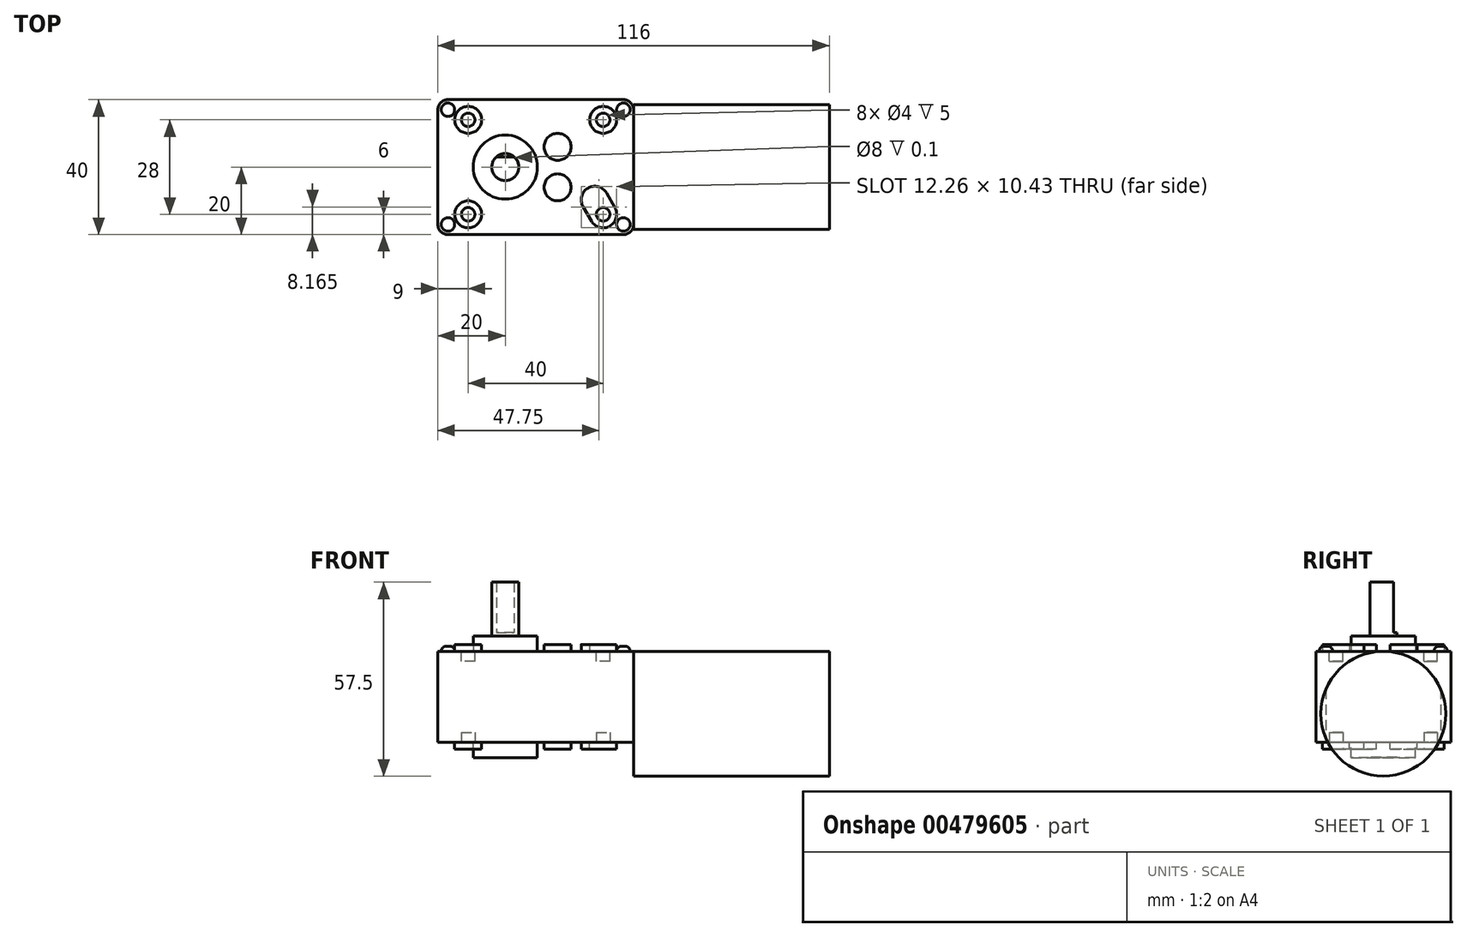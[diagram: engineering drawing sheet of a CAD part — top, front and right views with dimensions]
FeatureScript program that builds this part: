
annotation { "Feature Type Name" : "Feature", "Feature Type Description" : "" }
export const myFeature = defineFeature(function(context is Context, id is Id, definition is map)
    precondition{}
    {
        {
            var Q0;
            Q0=qCreatedBy(makeId("Top.planeOp"),FACE);
            var sketch = newSketch(context, id + "F0", { "sketchPlane" : qUnion([Q0])});
            skLineSegment(sketch, "E0.bottom", {"start": v(35, 20) * mm, "end": v(-17, 20) * mm});
            skLineSegment(sketch, "E0.top", {"start": v(35, -20) * mm, "end": v(-17, -20) * mm});
            skLineSegment(sketch, "E0.left", {"start": v(38, 17) * mm, "end": v(38, -17) * mm});
            skLineSegment(sketch, "E0.right", {"start": v(-20, 17) * mm, "end": v(-20, -17) * mm});
            skPoint(sketch, "E0.middle", {"position": v(9, 0) * mm});
            skPoint(sketch, "E1.visualSharp", {"position": v(-20, 20) * mm});
            skArc(sketch, "E1.filletArc", {"start": v(-17, 20) * mm, "mid": v(-19.12, 19.12) * mm, "end": v(-20, 17) * mm});
            skPoint(sketch, "E2.visualSharp", {"position": v(-20, -20) * mm});
            skArc(sketch, "E2.filletArc", {"start": v(-20, -17) * mm, "mid": v(-19.12, -19.12) * mm, "end": v(-17, -20) * mm});
            skPoint(sketch, "E3.visualSharp", {"position": v(38, -20) * mm});
            skArc(sketch, "E3.filletArc", {"start": v(35, -20) * mm, "mid": v(37.12, -19.12) * mm, "end": v(38, -17) * mm});
            skPoint(sketch, "E4.visualSharp", {"position": v(38, 20) * mm});
            skArc(sketch, "E4.filletArc", {"start": v(38, 17) * mm, "mid": v(37.12, 19.12) * mm, "end": v(35, 20) * mm});
            skSolve(sketch);
        }
        {
            var Q0;
            Q0 = qSketchRegion(id + "F0", true);
            extrude(context, id + "F1", {"entities" : qUnion([Q0]), "depth" : 27 * mm});
        }
        {
            var Q0;
            Q0=makeQuery(id+"F1.opExtrude","CAP_FACE",FACE,{"disambiguationData":[OSD([sQuery(id+"F0.wireOp",EDGE,"E0.bottom"),sQuery(id+"F0.wireOp",EDGE,"E0.top"),sQuery(id+"F0.wireOp",EDGE,"E0.left"),sQuery(id+"F0.wireOp",EDGE,"E0.right"),sQuery(id+"F0.wireOp",EDGE,"E1.filletArc"),sQuery(id+"F0.wireOp",EDGE,"E2.filletArc"),sQuery(id+"F0.wireOp",EDGE,"E3.filletArc"),sQuery(id+"F0.wireOp",EDGE,"E4.filletArc")])],"isStart":false});
            var sketch = newSketch(context, id + "F2", { "sketchPlane" : qUnion([Q0])});
            skLineSegment(sketch, "E5.bottom", {"start": v(-11, 14) * mm, "end": v(29, 14) * mm, "construction": true});
            skLineSegment(sketch, "E5.top", {"start": v(-11, -14) * mm, "end": v(29, -14) * mm, "construction": true});
            skLineSegment(sketch, "E5.left", {"start": v(-11, 14) * mm, "end": v(-11, -14) * mm, "construction": true});
            skLineSegment(sketch, "E5.right", {"start": v(29, 14) * mm, "end": v(29, -14) * mm, "construction": true});
            skPoint(sketch, "E5.middle", {"position": v(9, 0) * mm});
            skPoint(sketch, "E5.middle.positionSnap0", {"position": v(9, 20) * mm});
            skPoint(sketch, "E5.centerSnap0", {"position": v(9, 20) * mm});
            skCircle(sketch, "E6", {"center": v(-11, 14) * mm, "radius": 4 * mm});
            skCircle(sketch, "E7", {"center": v(29, 14) * mm, "radius": 4 * mm});
            skCircle(sketch, "E8", {"center": v(-11, -14) * mm, "radius": 4 * mm});
            skArc(sketch, "E9", {"start": v(29.96, -7.67) * mm, "mid": v(24.5, -6.2) * mm, "end": v(23.04, -11.67) * mm});
            skLineSegment(sketch, "E10", {"start": v(23.04, -11.67) * mm, "end": v(25.54, -16) * mm});
            skArc(sketch, "E11.trimOffspring", {"start": v(25.54, -16) * mm, "mid": v(31, -17.46) * mm, "end": v(32.46, -12) * mm});
            skLineSegment(sketch, "E12.trimOffspring", {"start": v(29.96, -7.67) * mm, "end": v(32.46, -12) * mm});
            skLineSegment(sketch, "E13", {"start": v(15.5, 14) * mm, "end": v(15.5, -14) * mm, "construction": true});
            skCircle(sketch, "E14", {"center": v(15.5, 6) * mm, "radius": 4 * mm});
            skCircle(sketch, "E15", {"center": v(15.5, -6) * mm, "radius": 4 * mm});
            skSolve(sketch);
        }
        {
            var Q0;
            Q0 = qSketchRegion(id + "F2", true);
            extrude(context, id + "F3", {"entities" : qUnion([Q0]), "operationType" : NewBodyOperationType.ADD, "depth" : 2 * mm});
        }
        {
            var Q0;
            Q0 = qSketchRegion(id + "F2", true);
            extrude(context, id + "F4", {"entities" : qUnion([Q0]), "operationType" : NewBodyOperationType.ADD, "oppositeDirection" : true, "depth" : 29 * mm});
        }
        {
            var Q0;
            Q0=makeQuery(id+"F1.opExtrude","CAP_FACE",FACE,{"disambiguationData":[OSD([sQuery(id+"F0.wireOp",EDGE,"E0.bottom"),sQuery(id+"F0.wireOp",EDGE,"E0.top"),sQuery(id+"F0.wireOp",EDGE,"E0.left"),sQuery(id+"F0.wireOp",EDGE,"E0.right"),sQuery(id+"F0.wireOp",EDGE,"E1.filletArc"),sQuery(id+"F0.wireOp",EDGE,"E2.filletArc"),sQuery(id+"F0.wireOp",EDGE,"E3.filletArc"),sQuery(id+"F0.wireOp",EDGE,"E4.filletArc")])],"isStart":false});
            var sketch = newSketch(context, id + "F5", { "sketchPlane" : qUnion([Q0])});
            skCircle(sketch, "E16", {"center": v(0, 0) * mm, "radius": 9.5 * mm});
            skSolve(sketch);
        }
        {
            var Q0;
            Q0 = qSketchRegion(id + "F5", true);
            extrude(context, id + "F6", {"entities" : qUnion([Q0]), "operationType" : NewBodyOperationType.ADD, "depth" : 4.5 * mm});
        }
        {
            var Q0;
            Q0 = qSketchRegion(id + "F5", true);
            extrude(context, id + "F7", {"entities" : qUnion([Q0]), "operationType" : NewBodyOperationType.ADD, "oppositeDirection" : true, "depth" : 31.5 * mm});
        }
        {
            var Q0;
            Q0=makeQuery(id+"F6.opExtrude","CAP_FACE",FACE,{"disambiguationData":[OSD([sQuery(id+"F5.wireOp",EDGE,"E16")])],"isStart":false});
            var sketch = newSketch(context, id + "F8", { "sketchPlane" : qUnion([Q0])});
            skCircle(sketch, "E17", {"center": v(0, 0) * mm, "radius": 4 * mm});
            skSolve(sketch);
        }
        {
            var Q0;
            Q0 = qSketchRegion(id + "F8", true);
            extrude(context, id + "F9", {"entities" : qUnion([Q0]), "operationType" : NewBodyOperationType.ADD, "depth" : 1 * mm});
        }
        {
            var Q0;
            Q0=makeQuery(id+"F9.opExtrude","CAP_FACE",FACE,{"disambiguationData":[OSD([sQuery(id+"F8.wireOp",EDGE,"E17")])],"isStart":false});
            var sketch = newSketch(context, id + "F10", { "sketchPlane" : qUnion([Q0])});
            skArc(sketch, "E18", {"start": v(-2.65, 3) * mm, "mid": v(0, -4) * mm, "end": v(2.65, 3) * mm});
            skLineSegment(sketch, "E19", {"start": v(-2.65, 3) * mm, "end": v(2.65, 3) * mm});
            skSolve(sketch);
        }
        {
            var Q0;
            Q0 = qSketchRegion(id + "F10", true);
            extrude(context, id + "F11", {"entities" : qUnion([Q0]), "operationType" : NewBodyOperationType.ADD, "depth" : 15 * mm});
        }
        {
            var Q0;
            Q0=makeQuery(id+"F7.opExtrude","CAP_FACE",FACE,{"disambiguationData":[OSD([sQuery(id+"F5.wireOp",EDGE,"E16")])],"isStart":false});
            var sketch = newSketch(context, id + "F12", { "sketchPlane" : qUnion([Q0])});
            skCircle(sketch, "E20", {"center": v(0, 0) * mm, "radius": 4 * mm});
            skSolve(sketch);
        }
        {
            var Q0;
            Q0 = qSketchRegion(id + "F12", true);
            extrude(context, id + "F13", {"entities" : qUnion([Q0]), "operationType" : NewBodyOperationType.REMOVE, "oppositeDirection" : true, "depth" : 0.1 * mm});
        }
        {
            var Q0;
            Q0=makeQuery(id+"F1.opExtrude","SWEPT_FACE",FACE,{"disambiguationData":[OSD([sQuery(id+"F0.wireOp",EDGE,"E0.left")])]});
            var sketch = newSketch(context, id + "F14", { "sketchPlane" : qUnion([Q0])});
            skCircle(sketch, "E21", {"center": v(0, 8.5) * mm, "radius": 18.5 * mm});
            skSolve(sketch);
        }
        {
            var Q0;
            Q0 = qSketchRegion(id + "F14", true);
            extrude(context, id + "F15", {"entities" : qUnion([Q0]), "operationType" : NewBodyOperationType.ADD, "depth" : 58 * mm});
        }
        {
            var Q0;
            Q0=makeQuery(id+"F1.opExtrude","CAP_FACE",FACE,{"disambiguationData":[OSD([sQuery(id+"F0.wireOp",EDGE,"E0.bottom"),sQuery(id+"F0.wireOp",EDGE,"E0.top"),sQuery(id+"F0.wireOp",EDGE,"E0.left"),sQuery(id+"F0.wireOp",EDGE,"E0.right"),sQuery(id+"F0.wireOp",EDGE,"E1.filletArc"),sQuery(id+"F0.wireOp",EDGE,"E2.filletArc"),sQuery(id+"F0.wireOp",EDGE,"E3.filletArc"),sQuery(id+"F0.wireOp",EDGE,"E4.filletArc")])],"isStart":false});
            var sketch = newSketch(context, id + "F16", { "sketchPlane" : qUnion([Q0])});
            skCircle(sketch, "E22", {"center": v(-17, 17) * mm, "radius": 2 * mm});
            skCircle(sketch, "E23", {"center": v(35, 17) * mm, "radius": 2 * mm});
            skCircle(sketch, "E24", {"center": v(35, -17) * mm, "radius": 2 * mm});
            skCircle(sketch, "E25", {"center": v(-17, -17) * mm, "radius": 2 * mm});
            skSolve(sketch);
        }
        {
            var Q0;
            Q0 = qSketchRegion(id + "F16", true);
            extrude(context, id + "F17", {"entities" : qUnion([Q0]), "operationType" : NewBodyOperationType.ADD, "depth" : 1.5 * mm});
        }
        {
            var Q0;
            Q0=makeQuery(id+"F17.opExtrude","CAP_EDGE",EDGE,{"disambiguationData":[OSD([sQuery(id+"F16.wireOp",EDGE,"E22")])],"isStart":false});
            var Q1;
            Q1=makeQuery(id+"F17.opExtrude","CAP_EDGE",EDGE,{"disambiguationData":[OSD([sQuery(id+"F16.wireOp",EDGE,"E25")])],"isStart":false});
            var Q2;
            Q2=makeQuery(id+"F17.opExtrude","CAP_EDGE",EDGE,{"disambiguationData":[OSD([sQuery(id+"F16.wireOp",EDGE,"E24")])],"isStart":false});
            var Q3;
            Q3=makeQuery(id+"F17.opExtrude","CAP_EDGE",EDGE,{"disambiguationData":[OSD([sQuery(id+"F16.wireOp",EDGE,"E23")])],"isStart":false});
            fillet(context, id + "F18", {"entities" : qUnion([Q0, Q1, Q2, Q3]), "radius" : 1.5 * mm, "tangentPropagation" : true, "allowEdgeOverflow" : false});
        }
        {
            var Q0;
            Q0=makeQuery(id+"F3.opExtrude","CAP_FACE",FACE,{"disambiguationData":[OSD([sQuery(id+"F2.wireOp",EDGE,"E6")])],"isStart":false});
            var sketch = newSketch(context, id + "F19", { "sketchPlane" : qUnion([Q0])});
            skCircle(sketch, "E26", {"center": v(-11, 14) * mm, "radius": 2 * mm});
            skCircle(sketch, "E27", {"center": v(-11, -14) * mm, "radius": 2 * mm});
            skCircle(sketch, "E28", {"center": v(29, -14) * mm, "radius": 2 * mm});
            skCircle(sketch, "E29", {"center": v(29, 14) * mm, "radius": 2 * mm});
            skSolve(sketch);
        }
        {
            var Q0;
            Q0 = qSketchRegion(id + "F19", true);
            extrude(context, id + "F20", {"entities" : qUnion([Q0]), "operationType" : NewBodyOperationType.REMOVE, "oppositeDirection" : true, "depth" : 5 * mm});
        }
        {
            var Q0;
            Q0=makeQuery(id+"F4.opExtrude","CAP_FACE",FACE,{"disambiguationData":[OSD([sQuery(id+"F2.wireOp",EDGE,"E9"),sQuery(id+"F2.wireOp",EDGE,"E10"),sQuery(id+"F2.wireOp",EDGE,"E11.trimOffspring"),sQuery(id+"F2.wireOp",EDGE,"E12.trimOffspring")])],"isStart":false});
            var sketch = newSketch(context, id + "F21", { "sketchPlane" : qUnion([Q0])});
            skCircle(sketch, "E30", {"center": v(29, 14) * mm, "radius": 2 * mm});
            skCircle(sketch, "E31", {"center": v(29, -14) * mm, "radius": 2 * mm});
            skCircle(sketch, "E32", {"center": v(-11, -14) * mm, "radius": 2 * mm});
            skCircle(sketch, "E33", {"center": v(-11, 14) * mm, "radius": 2 * mm});
            skSolve(sketch);
        }
        {
            var Q0;
            Q0 = qSketchRegion(id + "F21", true);
            extrude(context, id + "F22", {"entities" : qUnion([Q0]), "operationType" : NewBodyOperationType.REMOVE, "oppositeDirection" : true, "depth" : 5 * mm});
        }
    });
